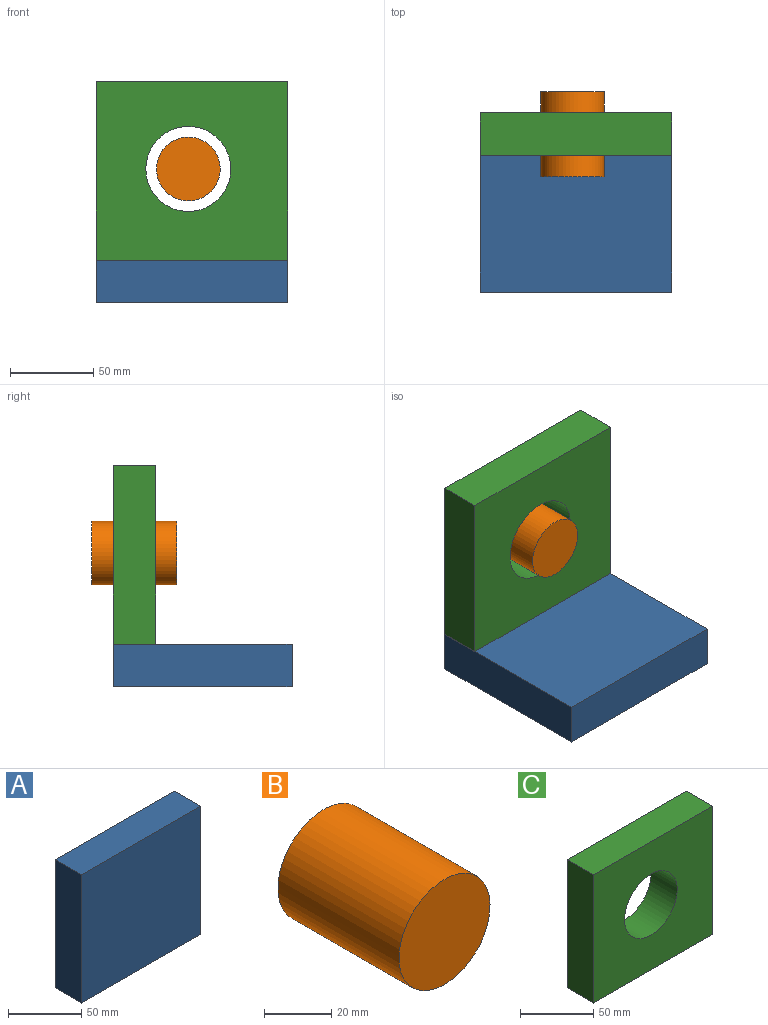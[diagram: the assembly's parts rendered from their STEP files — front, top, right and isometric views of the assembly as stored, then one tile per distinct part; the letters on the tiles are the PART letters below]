
ASSEMBLY  parts=3 mates=5
PART A: 6 faces, bbox 115x25.4x107.2 mm
  f0: plane 115.01x25.4mm, normal (0,0,1), area 2921.4mm2, adj f1,f3,f4,f5
  f1: plane 107.2x25.4mm, normal (-1,0,0), area 2722.9mm2, adj f0,f2,f4,f5
  f2: plane 115.01x25.4mm, normal (0,0,-1), area 2921.4mm2, adj f1,f3,f4,f5
  f3: plane 107.2x25.4mm, normal (1,0,0), area 2722.9mm2, adj f0,f2,f4,f5
  f4: plane 115.01x107.2mm, normal (0,-1,0), area 12329.6mm2, adj f0,f1,f2,f3
  f5: plane 115.01x107.2mm, normal (0,1,0), area 12329.6mm2, adj f0,f1,f2,f3
PART B: 3 faces, bbox 38.2x50.8x38.2 mm
  f0: cylinder r=19.09mm len=50.8mm, axis (0,1,0), area 6094.6mm2, adj f1,f2
  f1: plane 38.19x38.19mm, normal (0,-1,0), area 1145.4mm2, adj f0
  f2: plane 38.19x38.19mm, normal (0,1,0), area 1145.4mm2, adj f0
PART C: 7 faces, bbox 115x25.4x107.2 mm
  f0: plane 115.01x25.4mm, normal (0,0,1), area 2921.4mm2, adj f1,f3,f4,f5
  f1: plane 107.2x25.4mm, normal (-1,0,0), area 2722.9mm2, adj f0,f2,f4,f5
  f2: plane 115.01x25.4mm, normal (0,0,-1), area 2921.4mm2, adj f1,f3,f4,f5
  f3: plane 107.2x25.4mm, normal (1,0,0), area 2722.9mm2, adj f0,f2,f4,f5
  f4: plane 115.01x107.2mm, normal (0,-1,0), area 10291.7mm2, adj f0,f1,f2,f3,f6
  f5: plane 115.01x107.2mm, normal (0,1,0), area 10291.7mm2, adj f0,f1,f2,f3,f6
  f6: cylinder r=25.47mm len=50.94mm, axis (0,-1,0), area 4064.8mm2, adj f4,f5
PLACE A rot(axis=(-1,0,0),90deg) t=(7.26,-40.39,-78.99)mm
PLACE B t=(5.07,25.91,1.1)mm
PLACE C t=(0.85,13.21,19.07)mm fixed
MATE cylindrical B.f0 <-> C.f6  axis (0,1,0) through (5.07,25.91,1.1)mm
MATE planar B.f0 <-> C.f6  axis (0,1,0) through (5.07,25.91,1.1)mm
MATE planar A.f4 <-> C.f2  axis (0,0,1) through (7.26,-40.39,-53.59)mm
MATE planar A.f0 <-> C.f6  axis (0,1,0) through (7.26,13.21,-66.29)mm
MATE planar A.f3 <-> C.f3  axis (1,0,0) through (64.77,-40.39,-66.29)mm
